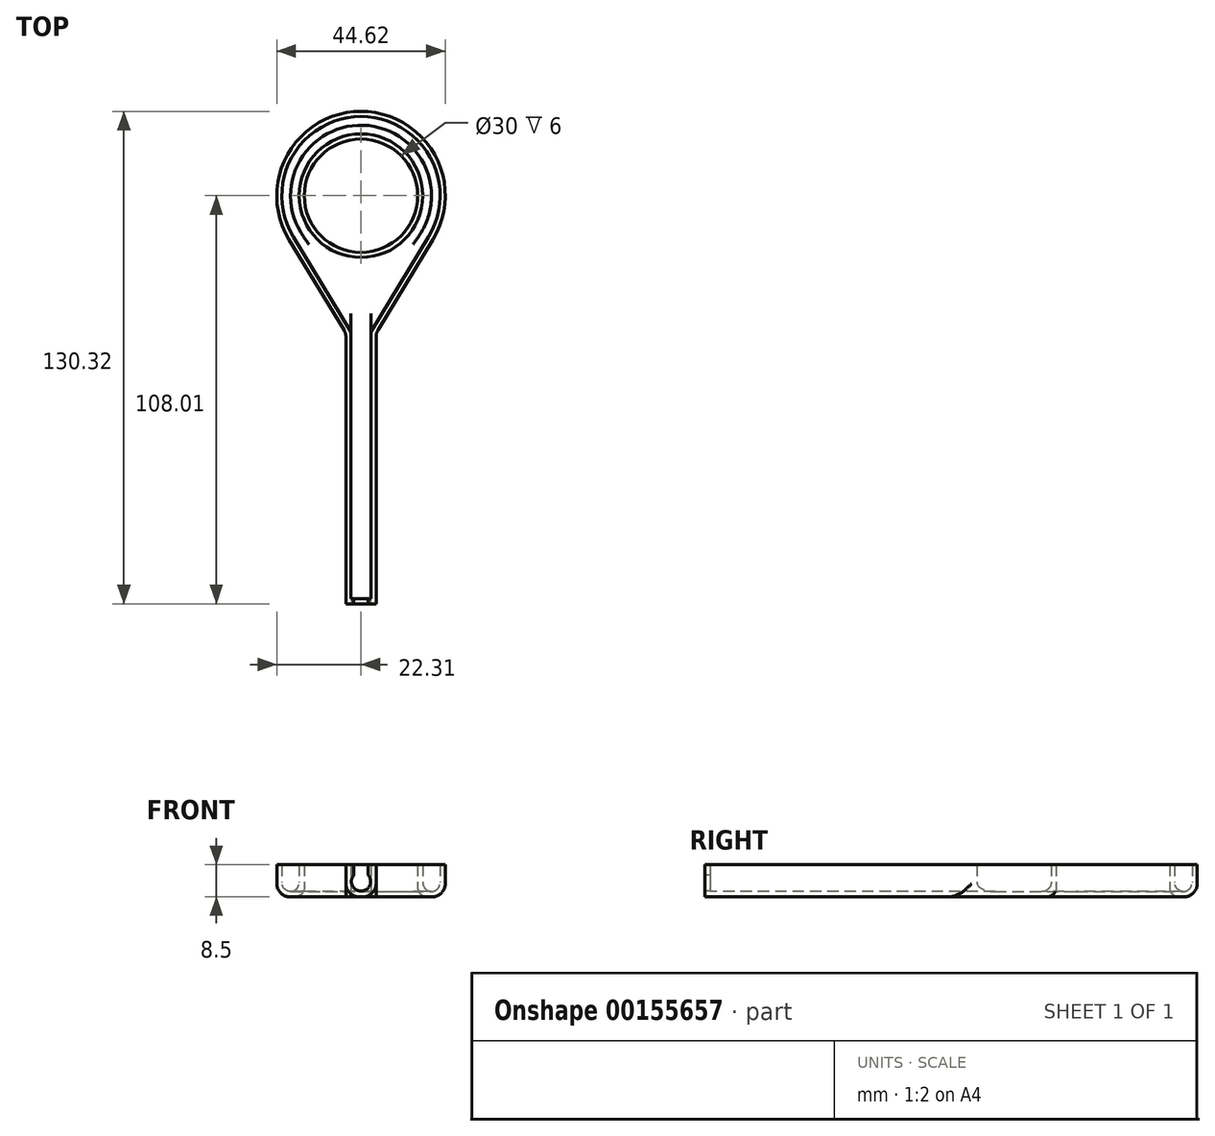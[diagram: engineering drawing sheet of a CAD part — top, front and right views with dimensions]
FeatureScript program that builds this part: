
annotation { "Feature Type Name" : "Feature", "Feature Type Description" : "" }
export const myFeature = defineFeature(function(context is Context, id is Id, definition is map)
    precondition{}
    {
        {
            var Q0;
            Q0=qCreatedBy(makeId("Top.planeOp"),FACE);
            var sketch = newSketch(context, id + "F0", { "sketchPlane" : qUnion([Q0])});
            skLineSegment(sketch, "E0.top", {"start": v(4, -108) * mm, "end": v(-4, -108) * mm});
            skPoint(sketch, "E0.middle", {"position": v(0, -54) * mm});
            skLineSegment(sketch, "E1", {"start": v(-4, -36.4) * mm, "end": v(-19.06, -11.58) * mm});
            skPoint(sketch, "E1.startSnap0", {"position": v(0.13, -36.4) * mm});
            skLineSegment(sketch, "E2.MirrorCS", {"start": v(4, -36.4) * mm, "end": v(19.06, -11.58) * mm});
            skPoint(sketch, "E3.orphan", {"position": v(4, -9.4) * mm});
            skPoint(sketch, "E4.orphan", {"position": v(-4, -9.4) * mm});
            skPoint(sketch, "E5.orphan", {"position": v(-2.58, 0) * mm});
            skPoint(sketch, "E0.bottom.start.orphan", {"position": v(2.58, 0) * mm});
            skArc(sketch, "E6.trimOffspring", {"start": v(19.06, -11.58) * mm, "mid": v(0, 22.3) * mm, "end": v(-19.06, -11.58) * mm});
            skLineSegment(sketch, "E7.trimOffspring", {"start": v(-4, -36.4) * mm, "end": v(-4, -108) * mm});
            skLineSegment(sketch, "E8.trimOffspring", {"start": v(4, -36.4) * mm, "end": v(4, -108) * mm});
            skPoint(sketch, "E9.orphan", {"position": v(10.6, -36.4) * mm});
            skPoint(sketch, "E10.orphan", {"position": v(-10.33, -36.4) * mm});
            skPoint(sketch, "E11.orphan", {"position": v(2.58, -108) * mm});
            skPoint(sketch, "E12.orphan", {"position": v(-2.58, -108) * mm});
            skPoint(sketch, "E13.orphan", {"position": v(-4, -111.4) * mm});
            skPoint(sketch, "E14.orphan", {"position": v(4, -111.4) * mm});
            skCircle(sketch, "E15", {"center": v(0, 0) * mm, "radius": 15 * mm});
            skSolve(sketch);
        }
        {
            var Q0;
            Q0 = qSketchRegion(id + "F0", true);
            extrude(context, id + "F1", {"entities" : qUnion([Q0]), "depth" : 8.5 * mm});
        }
        {
            var Q0;
            Q0=makeQuery(id+"F1.opExtrude","CAP_FACE",FACE,{"disambiguationData":[OSD([sQuery(id+"F0.wireOp",EDGE,"E0.top"),sQuery(id+"F0.wireOp",EDGE,"E1"),sQuery(id+"F0.wireOp",EDGE,"E2.MirrorCS"),sQuery(id+"F0.wireOp",EDGE,"E6.trimOffspring"),sQuery(id+"F0.wireOp",EDGE,"E7.trimOffspring"),sQuery(id+"F0.wireOp",EDGE,"E8.trimOffspring"),sQuery(id+"F0.wireOp",EDGE,"E15")])],"isStart":false});
            shell(context, id + "F2", {"entities" : qUnion([Q0]), "thickness" : 1.35 * mm});
        }
        {
            var Q0;
            Q0=makeQuery(id+"F1.opExtrude","SWEPT_FACE",FACE,{"disambiguationData":[OSD([sQuery(id+"F0.wireOp",EDGE,"E0.top")])]});
            var sketch = newSketch(context, id + "F3", { "sketchPlane" : qUnion([Q0])});
            skArc(sketch, "E16", {"start": v(-1.93, 5.72) * mm, "mid": v(0, 1.5) * mm, "end": v(1.93, 5.72) * mm});
            skLineSegment(sketch, "E17.bottom", {"start": v(1.93, 8.5) * mm, "end": v(-1.93, 8.5) * mm});
            skLineSegment(sketch, "E17.left", {"start": v(1.93, 8.5) * mm, "end": v(1.93, 5.72) * mm});
            skLineSegment(sketch, "E17.right", {"start": v(-1.93, 8.5) * mm, "end": v(-1.93, 5.72) * mm});
            skPoint(sketch, "E17.middle", {"position": v(0, 5.79) * mm});
            skPoint(sketch, "E17.top.end.orphan", {"position": v(-1.93, 3.08) * mm});
            skPoint(sketch, "E18.orphan", {"position": v(1.93, 3.08) * mm});
            skSolve(sketch);
        }
        {
            var Q0;
            Q0 = qSketchRegion(id + "F3", true);
            extrude(context, id + "F4", {"entities" : qUnion([Q0]), "operationType" : NewBodyOperationType.REMOVE, "oppositeDirection" : true, "depth" : 80 * mm});
        }
        {
            var Q0;
            Q0=makeQuery(id+"F1.opExtrude","SWEPT_EDGE",EDGE,{"disambiguationData":[OSD([sQuery(id+"F0.wireOp",EDGE,"E2.MirrorCS"),sQuery(id+"F0.wireOp",EDGE,"E8.trimOffspring")])]});
            var Q1;
            Q1=makeQuery(id+"F1.opExtrude","SWEPT_EDGE",EDGE,{"disambiguationData":[OSD([sQuery(id+"F0.wireOp",EDGE,"E1"),sQuery(id+"F0.wireOp",EDGE,"E7.trimOffspring")])]});
            var Q2;
            Q2=makeQuery(id+"F1.opExtrude","CAP_EDGE",EDGE,{"disambiguationData":[OSD([sQuery(id+"F0.wireOp",EDGE,"E1")])],"isStart":true});
            fillet(context, id + "F5", {"entities" : qUnion([Q0, Q1, Q2]), "radius" : 3.5 * mm, "tangentPropagation" : true, "allowEdgeOverflow" : false});
        }
        {
            var Q0;
            {var subQ0=sQuery(id+"F0.wireOp",EDGE,"E6.trimOffspring");Q0=makeQuery(id+"F2.opShell","OFFSET_EDGE",EDGE,{"disambiguationData":[OSD([subQ0]),TDD([makeQuery(id+"F1.opExtrude","CAP_EDGE",EDGE,{"disambiguationData":[OSD([subQ0])],"isStart":true})])]});}
            var Q1;
            {var subQ0=sQuery(id+"F0.wireOp",EDGE,"E15");Q1=makeQuery(id+"F2.opShell","OFFSET_EDGE",EDGE,{"disambiguationData":[OSD([subQ0]),TDD([makeQuery(id+"F1.opExtrude","CAP_EDGE",EDGE,{"disambiguationData":[OSD([subQ0])],"isStart":true})])]});}
            var Q2;
            Q2=makeQuery(id+"F1.opExtrude","CAP_EDGE",EDGE,{"disambiguationData":[OSD([sQuery(id+"F0.wireOp",EDGE,"E15")])],"isStart":true});
            fillet(context, id + "F6", {"entities" : qUnion([Q0, Q1, Q2]), "radius" : 2.5 * mm, "tangentPropagation" : true, "allowEdgeOverflow" : false});
        }
    });
